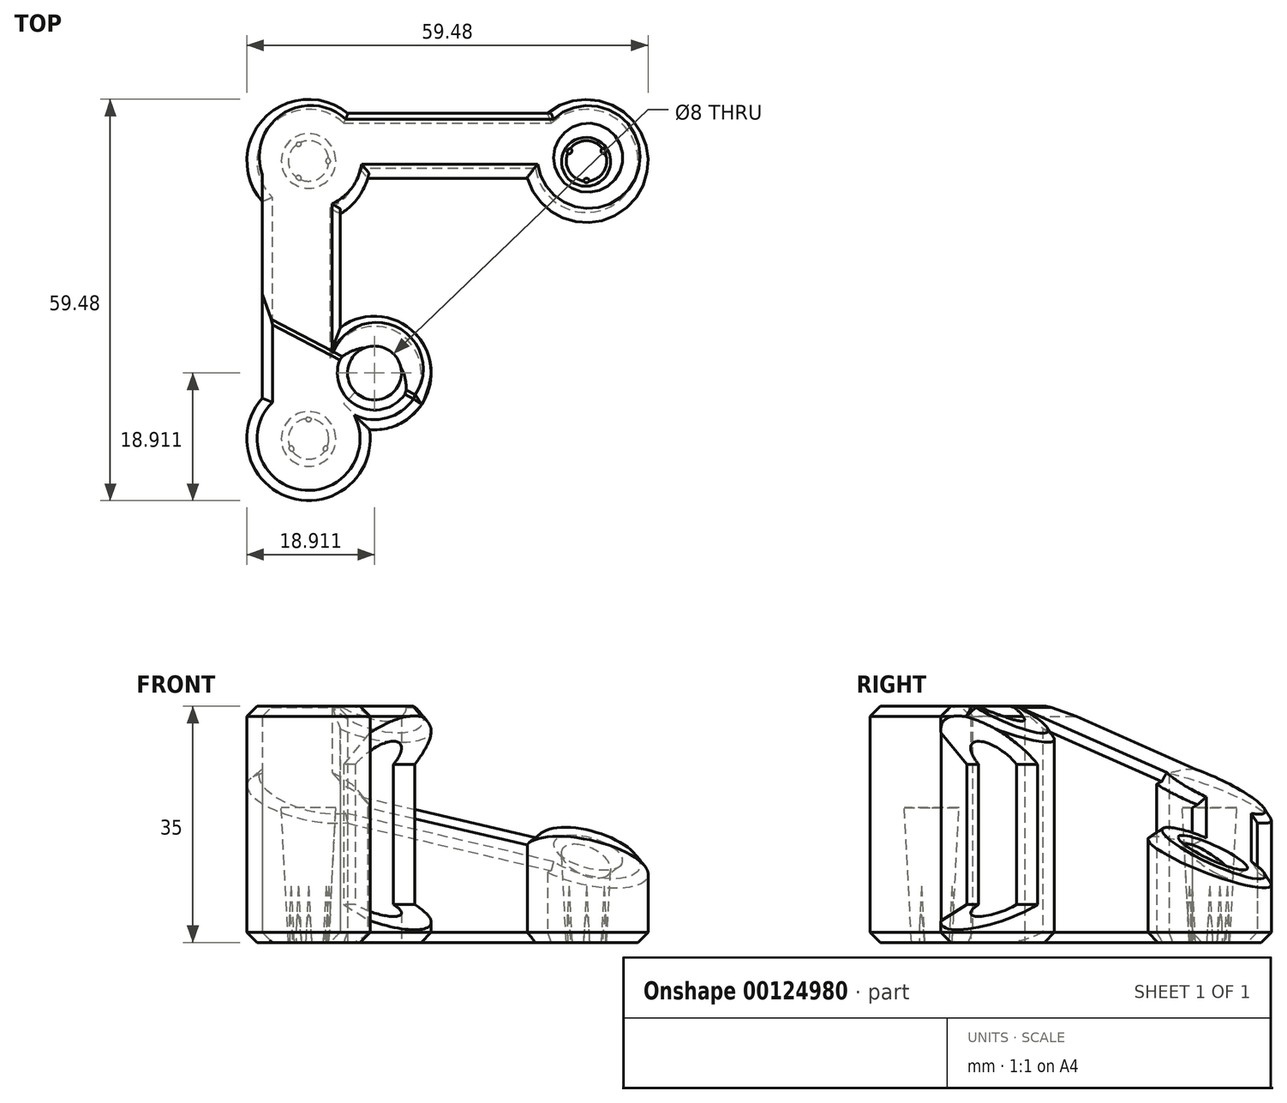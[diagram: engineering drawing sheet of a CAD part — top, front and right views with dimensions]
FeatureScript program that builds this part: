
annotation { "Feature Type Name" : "Feature", "Feature Type Description" : "" }
export const myFeature = defineFeature(function(context is Context, id is Id, definition is map)
    precondition{}
    {
        {
            var Q0;
            Q0=qCreatedBy(makeId("Top.planeOp"),FACE);
            var sketch = newSketch(context, id + "F0", { "sketchPlane" : qUnion([Q0])});
            skLineSegment(sketch, "E0.bottom", {"start": v(20.6, -20.6) * mm, "end": v(-20.6, -20.6) * mm, "construction": true});
            skLineSegment(sketch, "E0.top", {"start": v(20.6, 20.6) * mm, "end": v(-20.6, 20.6) * mm, "construction": true});
            skLineSegment(sketch, "E0.left", {"start": v(20.6, -20.6) * mm, "end": v(20.6, 20.6) * mm, "construction": true});
            skLineSegment(sketch, "E0.right", {"start": v(-20.6, -20.6) * mm, "end": v(-20.6, 20.6) * mm, "construction": true});
            skPoint(sketch, "E0.middle", {"position": v(0, 0) * mm});
            skCircle(sketch, "E1", {"center": v(-20.6, 20.6) * mm, "radius": 3 * mm});
            skLineSegment(sketch, "E2.bottom", {"start": v(10.83, -10.83) * mm, "end": v(-10.83, -10.83) * mm, "construction": true});
            skLineSegment(sketch, "E2.top", {"start": v(10.83, 10.83) * mm, "end": v(-10.83, 10.83) * mm, "construction": true});
            skLineSegment(sketch, "E2.left", {"start": v(10.83, -10.83) * mm, "end": v(10.83, 10.83) * mm, "construction": true});
            skLineSegment(sketch, "E2.right", {"start": v(-10.83, -10.83) * mm, "end": v(-10.83, 10.83) * mm, "construction": true});
            skCircle(sketch, "E3", {"center": v(-20.6, 20.6) * mm, "radius": 9.14 * mm});
            skCircle(sketch, "E4.1.0", {"center": v(-20.6, -20.6) * mm, "radius": 9.14 * mm});
            skCircle(sketch, "E4.1.1", {"center": v(-20.6, -20.6) * mm, "radius": 3 * mm});
            skCircle(sketch, "E4.2.0", {"center": v(20.6, -20.6) * mm, "radius": 9.14 * mm});
            skCircle(sketch, "E4.2.1", {"center": v(20.6, -20.6) * mm, "radius": 3 * mm});
            skCircle(sketch, "E4.3.0", {"center": v(20.6, 20.6) * mm, "radius": 9.14 * mm});
            skCircle(sketch, "E4.3.1", {"center": v(20.6, 20.6) * mm, "radius": 3 * mm});
            skCircle(sketch, "E5", {"center": v(-10.83, -10.83) * mm, "radius": 4 * mm});
            skCircle(sketch, "E6", {"center": v(-17.6, 20.6) * mm, "radius": 0.44 * mm});
            skCircle(sketch, "E7.1.0", {"center": v(-22.1, 23.2) * mm, "radius": 0.44 * mm});
            skCircle(sketch, "E7.2.0", {"center": v(-22.1, 18) * mm, "radius": 0.44 * mm});
            skCircle(sketch, "E8.1.0", {"center": v(-18, -22.1) * mm, "radius": 0.44 * mm});
            skCircle(sketch, "E8.1.1", {"center": v(-20.6, -17.6) * mm, "radius": 0.44 * mm});
            skCircle(sketch, "E8.1.2", {"center": v(-23.2, -22.1) * mm, "radius": 0.44 * mm});
            skCircle(sketch, "E8.2.0", {"center": v(22.1, -18) * mm, "radius": 0.44 * mm});
            skCircle(sketch, "E8.2.1", {"center": v(17.6, -20.6) * mm, "radius": 0.44 * mm});
            skCircle(sketch, "E8.2.2", {"center": v(22.1, -23.2) * mm, "radius": 0.44 * mm});
            skCircle(sketch, "E8.3.0", {"center": v(18, 22.1) * mm, "radius": 0.44 * mm});
            skCircle(sketch, "E8.3.1", {"center": v(20.6, 17.6) * mm, "radius": 0.44 * mm});
            skCircle(sketch, "E8.3.2", {"center": v(23.2, 22.1) * mm, "radius": 0.44 * mm});
            skSolve(sketch);
        }
        {
            var Q0;
            Q0=qCreatedBy(makeId("Top.planeOp"),FACE);
            var sketch = newSketch(context, id + "F1", { "sketchPlane" : qUnion([Q0])});
            skCircle(sketch, "E9", {"center": v(-10.83, -10.83) * mm, "radius": 8.42 * mm});
            skCircle(sketch, "E10", {"center": v(-20.6, -20.6) * mm, "radius": 9.14 * mm});
            skLineSegment(sketch, "E11", {"start": v(-13.5, -26.34) * mm, "end": v(13.66, -26.34) * mm, "construction": true});
            skLineSegment(sketch, "E12", {"start": v(13.66, -26.34) * mm, "end": v(13.66, -18.3) * mm, "construction": true});
            skLineSegment(sketch, "E13", {"start": v(13.66, -18.3) * mm, "end": v(-11.76, -18.3) * mm, "construction": true});
            skCircle(sketch, "E14.1.0", {"center": v(-20.6, 20.6) * mm, "radius": 9.14 * mm});
            skPoint(sketch, "E14.center", {"position": v(0, 0) * mm});
            skLineSegment(sketch, "E14.anchor1", {"start": v(0, 0) * mm, "end": v(-20.6, -20.6) * mm, "construction": true});
            skLineSegment(sketch, "E14.anchor2", {"start": v(0, 0) * mm, "end": v(20.6, 20.6) * mm, "construction": true});
            skLineSegment(sketch, "E15", {"start": v(-27.47, 14.57) * mm, "end": v(-27.47, -14.57) * mm});
            skLineSegment(sketch, "E16", {"start": v(-15.92, 12.75) * mm, "end": v(-15.92, -4.13) * mm});
            skCircle(sketch, "E17.1.2.0", {"center": v(20.6, 20.6) * mm, "radius": 9.14 * mm});
            skLineSegment(sketch, "E18", {"start": v(-11.84, 18) * mm, "end": v(11.84, 18) * mm});
            skLineSegment(sketch, "E19", {"start": v(-14.84, 27.7) * mm, "end": v(14.84, 27.7) * mm});
            skSolve(sketch);
        }
        {
            var Q0;
            {var subQ0=sQuery(id+"F1.wireOp",EDGE,"E15");Q0=makeQuery(id+"F1.imprint","IMPRINT",FACE,{"disambiguationData":[TD([[makeQuery(id+"F1.imprint","IMPRINT",EDGE,{"derivedFrom":subQ0}),1.0]])]});}
            var Q1;
            {var subQ0=sQuery(id+"F1.wireOp",EDGE,"E9");var subQ1=makeQuery(id+"F1.imprint","INTERSECT",VERTEX,{"derivedFrom":[subQ0,sQuery(id+"F1.wireOp",EDGE,"E16")]});Q1=makeQuery(id+"F1.imprint","IMPRINT",FACE,{"disambiguationData":[TD([[makeQuery(id+"F1.imprint","IMPRINT",EDGE,{"disambiguationData":[TD([[subQ1,-1.0]])],"derivedFrom":subQ0}),1.0]])]});}
            var Q2;
            {var subQ0=sQuery(id+"F1.wireOp",EDGE,"E10");var subQ1=sQuery(id+"F1.wireOp",EDGE,"E9");var subQ2=makeQuery(id+"F1.imprint","INTERSECT",VERTEX,{"disambiguationData":[OD(0.0)],"derivedFrom":[subQ1,subQ0]});Q2=makeQuery(id+"F1.imprint","IMPRINT",FACE,{"disambiguationData":[TD([[makeQuery(id+"F1.imprint","IMPRINT",EDGE,{"disambiguationData":[TD([[subQ2,1.0]])],"derivedFrom":subQ1}),-1.0]])]});}
            var Q3;
            {var subQ0=sQuery(id+"F1.wireOp",EDGE,"E10");var subQ1=sQuery(id+"F1.wireOp",EDGE,"E9");var subQ2=makeQuery(id+"F1.imprint","INTERSECT",VERTEX,{"disambiguationData":[OD(0.0)],"derivedFrom":[subQ1,subQ0]});Q3=makeQuery(id+"F1.imprint","IMPRINT",FACE,{"disambiguationData":[TD([[makeQuery(id+"F1.imprint","IMPRINT",EDGE,{"disambiguationData":[TD([[subQ2,1.0]])],"derivedFrom":subQ1}),1.0]])]});}
            var Q4;
            {var subQ0=sQuery(id+"F1.wireOp",EDGE,"E14.1.0");var subQ1=makeQuery(id+"F1.imprint","INTERSECT",VERTEX,{"derivedFrom":[subQ0,sQuery(id+"F1.wireOp",EDGE,"E15")]});Q4=makeQuery(id+"F1.imprint","IMPRINT",FACE,{"disambiguationData":[TD([[makeQuery(id+"F1.imprint","IMPRINT",EDGE,{"disambiguationData":[TD([[subQ1,1.0]])],"derivedFrom":subQ0}),1.0]])]});}
            var Q5;
            {var subQ0=sQuery(id+"F1.wireOp",EDGE,"E18");Q5=makeQuery(id+"F1.imprint","IMPRINT",FACE,{"disambiguationData":[TD([[makeQuery(id+"F1.imprint","IMPRINT",EDGE,{"derivedFrom":subQ0}),1.0]])]});}
            var Q6;
            {var subQ0=sQuery(id+"F1.wireOp",EDGE,"E17.1.2.0");var subQ1=makeQuery(id+"F1.imprint","INTERSECT",VERTEX,{"derivedFrom":[subQ0,sQuery(id+"F1.wireOp",EDGE,"E18")]});Q6=makeQuery(id+"F1.imprint","IMPRINT",FACE,{"disambiguationData":[TD([[makeQuery(id+"F1.imprint","IMPRINT",EDGE,{"disambiguationData":[TD([[subQ1,1.0]])],"derivedFrom":subQ0}),1.0]])]});}
            extrude(context, id + "F2", {"entities" : qUnion([Q0, Q1, Q2, Q3, Q4, Q5, Q6]), "depth" : 35 * mm});
        }
        {
            var Q0;
            Q0=makeQuery(id+"F0.imprint","IMPRINT",FACE,{"disambiguationData":[TD([[makeQuery(id+"F0.imprint","IMPRINT",EDGE,{"derivedFrom":sQuery(id+"F0.wireOp",EDGE,"E5")}),1.0]])]});
            extrude(context, id + "F3", {"entities" : qUnion([Q0]), "operationType" : NewBodyOperationType.REMOVE, "endBound" : BoundingType.THROUGH_ALL, "depth" : 25 * mm});
        }
        {
            var Q0;
            Q0=makeQuery(id+"F0.imprint","IMPRINT",FACE,{"disambiguationData":[TD([[makeQuery(id+"F0.imprint","IMPRINT",EDGE,{"derivedFrom":sQuery(id+"F0.wireOp",EDGE,"E4.1.1")}),1.0]])]});
            var Q1;
            Q1=makeQuery(id+"F0.imprint","IMPRINT",FACE,{"disambiguationData":[TD([[makeQuery(id+"F0.imprint","IMPRINT",EDGE,{"derivedFrom":sQuery(id+"F0.wireOp",EDGE,"E1")}),1.0]])]});
            var Q2;
            Q2=makeQuery(id+"F0.imprint","IMPRINT",FACE,{"disambiguationData":[TD([[makeQuery(id+"F0.imprint","IMPRINT",EDGE,{"derivedFrom":sQuery(id+"F0.wireOp",EDGE,"E4.3.1")}),1.0]])]});
            extrude(context, id + "F4", {"entities" : qUnion([Q0, Q1, Q2]), "operationType" : NewBodyOperationType.REMOVE, "depth" : 20 * mm, "hasDraft" : true, "draftAngle" : 3 * degree});
        }
        {
            var Q0;
            Q0=qCreatedBy(makeId("Right.planeOp"),FACE);
            var Q1;
            Q1=makeQuery(id+"F2.opExtrude","SWEPT_EDGE",EDGE,{"disambiguationData":[OSD([sQuery(id+"F1.wireOp",EDGE,"E9"),sQuery(id+"F1.wireOp",EDGE,"E10")])]});
            cPlane(context, id + "F5", {"entities" : qUnion([Q0, Q1]), "cplaneType" : CPlaneType.LINE_ANGLE, "offset" : 25 * mm, "angle" : 45 * degree, "oppositeDirection" : true, "width" : 150 * mm, "height" : 150 * mm});
        }
        {
            var Q0;
            Q0=qCreatedBy(id+"F5.planeOp",FACE);
            var sketch = newSketch(context, id + "F6", { "sketchPlane" : qUnion([Q0])});
            skLineSegment(sketch, "E20", {"start": v(10.06, 35.01) * mm, "end": v(0, 26.4) * mm});
            skLineSegment(sketch, "E21", {"start": v(0, 26.4) * mm, "end": v(0, 5.63) * mm});
            skLineSegment(sketch, "E22", {"start": v(0, 5.63) * mm, "end": v(10.06, 1.15) * mm});
            skLineSegment(sketch, "E23", {"start": v(10.06, 1.15) * mm, "end": v(10.06, 35.01) * mm});
            skSolve(sketch);
        }
        {
            var Q0;
            Q0 = qSketchRegion(id + "F6", true);
            extrude(context, id + "F7", {"entities" : qUnion([Q0]), "operationType" : NewBodyOperationType.REMOVE, "oppositeDirection" : true, "depth" : 25 * mm});
        }
        {
            var Q0;
            Q0=qCreatedBy(makeId("Right.planeOp"),FACE);
            var sketch = newSketch(context, id + "F8", { "sketchPlane" : qUnion([Q0])});
            skLineSegment(sketch, "E24.bottom", {"start": v(-25.5, 73.77) * mm, "end": v(54.17, 56.4) * mm});
            skLineSegment(sketch, "E24.top", {"start": v(-20.3, 36.5) * mm, "end": v(62.05, 0) * mm});
            skLineSegment(sketch, "E24.left", {"start": v(-25.5, 73.77) * mm, "end": v(-20.3, 36.5) * mm});
            skLineSegment(sketch, "E24.right", {"start": v(54.17, 56.4) * mm, "end": v(62.05, 0) * mm});
            skSolve(sketch);
        }
        {
            var Q0;
            Q0 = qSketchRegion(id + "F8", true);
            extrude(context, id + "F9", {"entities" : qUnion([Q0]), "operationType" : NewBodyOperationType.REMOVE, "endBound" : BoundingType.THROUGH_ALL, "oppositeDirection" : true, "depth" : 25 * mm, "hasDraft" : true, "draftAngle" : 12 * degree, "draftPullDirection" : true, "hasSecondDirection" : true, "secondDirectionBound" : BoundingType.THROUGH_ALL, "secondDirectionOppositeDirection" : false, "secondDirectionDepth" : 25 * mm, "hasSecondDirectionDraft" : true, "secondDirectionDraftAngle" : 12 * degree});
        }
        {
            var Q0;
            Q0=makeQuery(id+"F2.opExtrude","CAP_FACE",FACE,{"disambiguationData":[OSD([sQuery(id+"F1.wireOp",EDGE,"E9"),sQuery(id+"F1.wireOp",EDGE,"E10"),sQuery(id+"F1.wireOp",EDGE,"E14.1.0"),sQuery(id+"F1.wireOp",EDGE,"E15"),sQuery(id+"F1.wireOp",EDGE,"E16"),sQuery(id+"F1.wireOp",EDGE,"E17.1.2.0"),sQuery(id+"F1.wireOp",EDGE,"E18"),sQuery(id+"F1.wireOp",EDGE,"E19")])],"isStart":false});
            var Q1;
            {var subQ0=makeQuery(id+"F9.opExtrude","SWEPT_FACE",FACE,{"disambiguationData":[OSD([sQuery(id+"F8.wireOp",EDGE,"E24.top")])]});Q1=makeQuery(id+"F9.boolean.opBoolean","INTERSECT",EDGE,{"derivedFrom":[makeQuery(id+"F2.opExtrude","SWEPT_FACE",FACE,{"disambiguationData":[OSD([sQuery(id+"F1.wireOp",EDGE,"E16")])]}),makeQuery(id+"F9.*.booleanUnion.opBoolean","MERGE",FACE,{"derivedFrom":[makeQuery(id+"F9.*.split.splitOp","SPLIT",FACE,{"derivedFrom":subQ0}),makeQuery(id+"F9.*.split.splitOp","SPLIT",FACE,{"derivedFrom":subQ0,"isFromBackBody":true})]})]});}
            var Q2;
            {var subQ0=makeQuery(id+"F9.opExtrude","SWEPT_FACE",FACE,{"disambiguationData":[OSD([sQuery(id+"F8.wireOp",EDGE,"E24.top")])]});Q2=makeQuery(id+"F9.boolean.opBoolean","INTERSECT",EDGE,{"derivedFrom":[makeQuery(id+"F2.opExtrude","SWEPT_FACE",FACE,{"disambiguationData":[OSD([sQuery(id+"F1.wireOp",EDGE,"E9")])]}),makeQuery(id+"F9.*.booleanUnion.opBoolean","MERGE",FACE,{"derivedFrom":[makeQuery(id+"F9.*.split.splitOp","SPLIT",FACE,{"derivedFrom":subQ0}),makeQuery(id+"F9.*.split.splitOp","SPLIT",FACE,{"derivedFrom":subQ0,"isFromBackBody":true})]})]});}
            var Q3;
            {var subQ0=makeQuery(id+"F9.opExtrude","SWEPT_FACE",FACE,{"disambiguationData":[OSD([sQuery(id+"F8.wireOp",EDGE,"E24.top")])]});var subQ1=sQuery(id+"F1.wireOp",EDGE,"E14.1.0");Q3=makeQuery(id+"F9.boolean.opBoolean","INTERSECT",EDGE,{"derivedFrom":[makeQuery(id+"F2.opExtrude","SWEPT_FACE",FACE,{"disambiguationData":[OSD([subQ1]),TDD([makeQuery(id+"F1.imprint","IMPRINT",EDGE,{"disambiguationData":[TD([[makeQuery(id+"F1.imprint","INTERSECT",VERTEX,{"derivedFrom":[subQ1,sQuery(id+"F1.wireOp",EDGE,"E16")]}),-1.0]])],"derivedFrom":subQ1})])]}),makeQuery(id+"F9.*.booleanUnion.opBoolean","MERGE",FACE,{"derivedFrom":[makeQuery(id+"F9.*.split.splitOp","SPLIT",FACE,{"derivedFrom":subQ0}),makeQuery(id+"F9.*.split.splitOp","SPLIT",FACE,{"derivedFrom":subQ0,"isFromBackBody":true})]})]});}
            var Q4;
            {var subQ0=makeQuery(id+"F9.opExtrude","SWEPT_FACE",FACE,{"disambiguationData":[OSD([sQuery(id+"F8.wireOp",EDGE,"E24.top")])]});Q4=makeQuery(id+"F9.boolean.opBoolean","INTERSECT",EDGE,{"derivedFrom":[makeQuery(id+"F2.opExtrude","SWEPT_FACE",FACE,{"disambiguationData":[OSD([sQuery(id+"F1.wireOp",EDGE,"E18")])]}),makeQuery(id+"F9.*.booleanUnion.opBoolean","MERGE",FACE,{"derivedFrom":[makeQuery(id+"F9.*.split.splitOp","SPLIT",FACE,{"derivedFrom":subQ0}),makeQuery(id+"F9.*.split.splitOp","SPLIT",FACE,{"derivedFrom":subQ0,"isFromBackBody":true})]})]});}
            var Q5;
            {var subQ0=makeQuery(id+"F9.opExtrude","SWEPT_FACE",FACE,{"disambiguationData":[OSD([sQuery(id+"F8.wireOp",EDGE,"E24.top")])]});Q5=makeQuery(id+"F9.boolean.opBoolean","INTERSECT",EDGE,{"derivedFrom":[makeQuery(id+"F2.opExtrude","SWEPT_FACE",FACE,{"disambiguationData":[OSD([sQuery(id+"F1.wireOp",EDGE,"E19")])]}),makeQuery(id+"F9.*.booleanUnion.opBoolean","MERGE",FACE,{"derivedFrom":[makeQuery(id+"F9.*.split.splitOp","SPLIT",FACE,{"derivedFrom":subQ0}),makeQuery(id+"F9.*.split.splitOp","SPLIT",FACE,{"derivedFrom":subQ0,"isFromBackBody":true})]})]});}
            var Q6;
            {var subQ0=makeQuery(id+"F9.opExtrude","SWEPT_FACE",FACE,{"disambiguationData":[OSD([sQuery(id+"F8.wireOp",EDGE,"E24.top")])]});var subQ1=sQuery(id+"F1.wireOp",EDGE,"E14.1.0");Q6=makeQuery(id+"F9.boolean.opBoolean","INTERSECT",EDGE,{"derivedFrom":[makeQuery(id+"F2.opExtrude","SWEPT_FACE",FACE,{"disambiguationData":[OSD([subQ1]),TDD([makeQuery(id+"F1.imprint","IMPRINT",EDGE,{"disambiguationData":[TD([[makeQuery(id+"F1.imprint","INTERSECT",VERTEX,{"derivedFrom":[subQ1,sQuery(id+"F1.wireOp",EDGE,"E15")]}),1.0]])],"derivedFrom":subQ1})])]}),makeQuery(id+"F9.*.booleanUnion.opBoolean","MERGE",FACE,{"derivedFrom":[makeQuery(id+"F9.*.split.splitOp","SPLIT",FACE,{"derivedFrom":subQ0}),makeQuery(id+"F9.*.split.splitOp","SPLIT",FACE,{"derivedFrom":subQ0,"isFromBackBody":true})]})]});}
            var Q7;
            {var subQ0=makeQuery(id+"F9.opExtrude","SWEPT_FACE",FACE,{"disambiguationData":[OSD([sQuery(id+"F8.wireOp",EDGE,"E24.top")])]});Q7=makeQuery(id+"F9.boolean.opBoolean","INTERSECT",EDGE,{"derivedFrom":[makeQuery(id+"F2.opExtrude","SWEPT_FACE",FACE,{"disambiguationData":[OSD([sQuery(id+"F1.wireOp",EDGE,"E17.1.2.0")])]}),makeQuery(id+"F9.*.booleanUnion.opBoolean","MERGE",FACE,{"derivedFrom":[makeQuery(id+"F9.*.split.splitOp","SPLIT",FACE,{"derivedFrom":subQ0}),makeQuery(id+"F9.*.split.splitOp","SPLIT",FACE,{"derivedFrom":subQ0,"isFromBackBody":true})]})]});}
            var Q8;
            {var subQ0=makeQuery(id+"F9.opExtrude","SWEPT_FACE",FACE,{"disambiguationData":[OSD([sQuery(id+"F8.wireOp",EDGE,"E24.top")])]});Q8=makeQuery(id+"F9.boolean.opBoolean","INTERSECT",EDGE,{"derivedFrom":[makeQuery(id+"F4.boolean.opBoolean","COPY",FACE,{"derivedFrom":makeQuery(id+"F4.opExtrude","SWEPT_FACE",FACE,{"disambiguationData":[OSD([sQuery(id+"F0.wireOp",EDGE,"E4.3.1")])]})}),makeQuery(id+"F9.*.booleanUnion.opBoolean","MERGE",FACE,{"derivedFrom":[makeQuery(id+"F9.*.split.splitOp","SPLIT",FACE,{"derivedFrom":subQ0}),makeQuery(id+"F9.*.split.splitOp","SPLIT",FACE,{"derivedFrom":subQ0,"isFromBackBody":true})]})]});}
            var Q9;
            Q9=makeQuery(id+"F2.opExtrude","CAP_EDGE",EDGE,{"disambiguationData":[OSD([sQuery(id+"F1.wireOp",EDGE,"E10")])],"isStart":true});
            var Q10;
            Q10=makeQuery(id+"F2.opExtrude","CAP_EDGE",EDGE,{"disambiguationData":[OSD([sQuery(id+"F1.wireOp",EDGE,"E9")])],"isStart":true});
            var Q11;
            Q11=makeQuery(id+"F2.opExtrude","CAP_EDGE",EDGE,{"disambiguationData":[OSD([sQuery(id+"F1.wireOp",EDGE,"E16")])],"isStart":true});
            var Q12;
            {var subQ0=sQuery(id+"F1.wireOp",EDGE,"E14.1.0");Q12=makeQuery(id+"F2.opExtrude","CAP_EDGE",EDGE,{"disambiguationData":[OSD([subQ0]),TDD([makeQuery(id+"F1.imprint","IMPRINT",EDGE,{"disambiguationData":[TD([[makeQuery(id+"F1.imprint","INTERSECT",VERTEX,{"derivedFrom":[subQ0,sQuery(id+"F1.wireOp",EDGE,"E16")]}),-1.0]])],"derivedFrom":subQ0})])],"isStart":true});}
            var Q13;
            Q13=makeQuery(id+"F2.opExtrude","CAP_EDGE",EDGE,{"disambiguationData":[OSD([sQuery(id+"F1.wireOp",EDGE,"E18")])],"isStart":true});
            var Q14;
            Q14=makeQuery(id+"F2.opExtrude","CAP_EDGE",EDGE,{"disambiguationData":[OSD([sQuery(id+"F1.wireOp",EDGE,"E17.1.2.0")])],"isStart":true});
            var Q15;
            Q15=makeQuery(id+"F2.opExtrude","CAP_EDGE",EDGE,{"disambiguationData":[OSD([sQuery(id+"F1.wireOp",EDGE,"E19")])],"isStart":true});
            var Q16;
            {var subQ0=sQuery(id+"F1.wireOp",EDGE,"E14.1.0");Q16=makeQuery(id+"F2.opExtrude","CAP_EDGE",EDGE,{"disambiguationData":[OSD([subQ0]),TDD([makeQuery(id+"F1.imprint","IMPRINT",EDGE,{"disambiguationData":[TD([[makeQuery(id+"F1.imprint","INTERSECT",VERTEX,{"derivedFrom":[subQ0,sQuery(id+"F1.wireOp",EDGE,"E15")]}),1.0]])],"derivedFrom":subQ0})])],"isStart":true});}
            var Q17;
            Q17=makeQuery(id+"F2.opExtrude","CAP_EDGE",EDGE,{"disambiguationData":[OSD([sQuery(id+"F1.wireOp",EDGE,"E15")])],"isStart":true});
            var Q18;
            Q18=makeQuery(id+"F3.boolean.opBoolean","COPY",EDGE,{"derivedFrom":makeQuery(id+"F3.opExtrude","CAP_EDGE",EDGE,{"disambiguationData":[OSD([sQuery(id+"F0.wireOp",EDGE,"E5")])],"isStart":true})});
            chamfer(context, id + "F10", {"entities" : qUnion([Q0, Q1, Q2, Q3, Q4, Q5, Q6, Q7, Q8, Q9, Q10, Q11, Q12, Q13, Q14, Q15, Q16, Q17, Q18]), "width" : 1.5 * mm, "tangentPropagation" : true});
        }
    });
